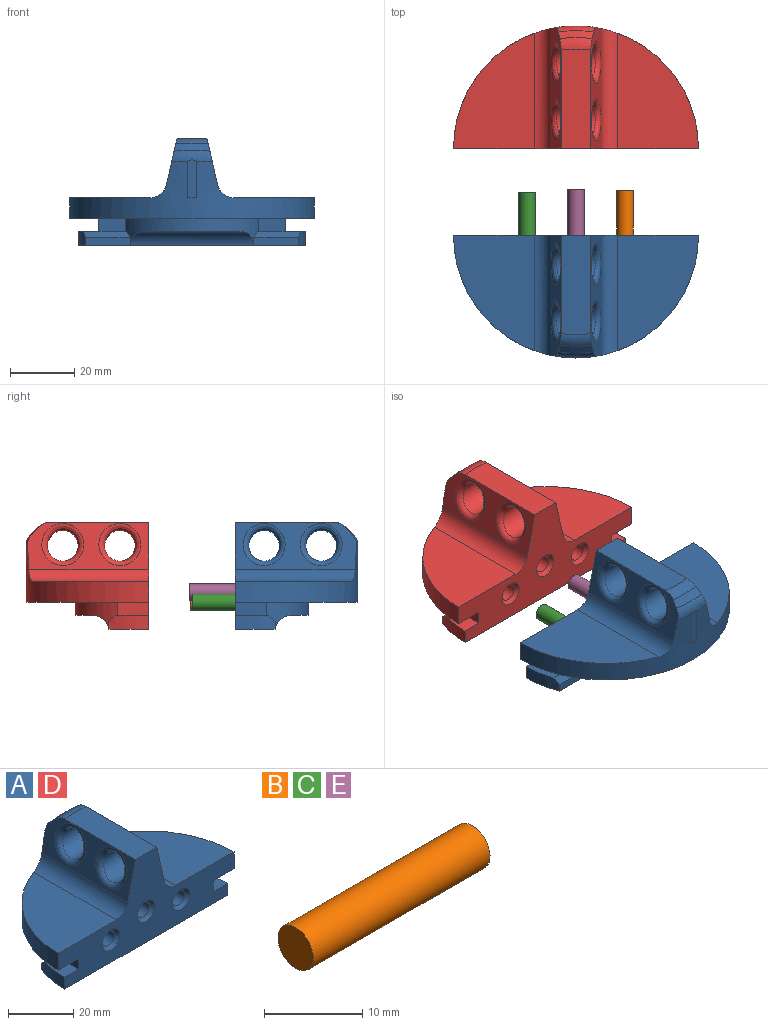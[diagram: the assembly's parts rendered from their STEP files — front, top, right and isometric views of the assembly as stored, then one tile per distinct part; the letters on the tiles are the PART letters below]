
ASSEMBLY  parts=5 mates=4
PART A: 46 faces, bbox 76.4x38.8x33.5 mm
  f0: plane 76.25x33.3mm, normal (0,-1,0), area 1152.4mm2, adj f10,f11,f12,f13,f14,f15,f16,f17
  f1: plane 29.8x5.52mm, normal (0,0,-1), area 112.7mm2, adj f6,f8
  f2: plane 2.76x0.03mm, normal (0,0,1), area 0mm2, adj f3,f25
  f3: plane 11.79x2.76mm, normal (0,1,0), area 32.2mm2, adj f2,f25,f38
  f4: plane 8.43x4.12mm, normal (0,1,0), area 34.7mm2, adj f6,f14,f15,f17
  f5: plane 8.43x4.12mm, normal (0,1,0), area 34.7mm2, adj f6,f13,f16,f17
  f6: cylinder r=22.86mm len=41.56mm, axis (0,0,-1), area 232mm2, adj f1,f4,f5,f7,f8,f9,f13,f14
  f7: plane 13.83x2.46mm, normal (0,1,0), area 34.1mm2, adj f6,f10,f11,f28
  f8: cylinder r=5.08mm len=38.53mm, axis (1,0,0), area 257.8mm2, adj f1,f6,f10
  f9: plane 13.83x2.46mm, normal (0,1,0), area 34.1mm2, adj f6,f10,f12,f27
  f10: plane 70.61x12.31mm, normal (0,0,-1), area 851mm2, adj f0,f7,f8,f9,f11,f12
  f11: cylinder r=35.31mm len=12.31mm, axis (0,0,-1), area 53mm2, adj f0,f7,f10,f13,f28
  f12: cylinder r=35.31mm len=12.31mm, axis (0,0,-1), area 53mm2, adj f0,f9,f10,f14,f27
  f13: plane 14.95x10.4mm, normal (0,0,1), area 65.6mm2, adj f0,f5,f6,f11,f16,f28
  f14: plane 14.95x10.4mm, normal (0,0,1), area 65.6mm2, adj f0,f4,f6,f12,f15,f27
  f15: plane 9.53x4.12mm, normal (-1,0,0), area 39.2mm2, adj f0,f4,f14,f17
  f16: plane 9.53x4.12mm, normal (1,0,0), area 39.2mm2, adj f0,f5,f13,f17
  f17: plane 76.25x38.13mm, normal (0,0,-1), area 1328.4mm2, adj f0,f4,f5,f6,f15,f16,f25
  f18: cylinder r=5.08mm len=37.28mm, axis (0,-1,0), area 249.8mm2, adj f0,f19,f20,f25
  f19: plane 37.78x14.7mm, normal (0.97,0,0.22), area 270mm2, adj f0,f18,f24,f25,f26,f38,f39,f42
  f20: plane 35.86x25.19mm, normal (0,0,1), area 658.2mm2, adj f0,f18,f25
  f21: cylinder r=5.08mm len=37.28mm, axis (0,1,0), area 249.8mm2, adj f0,f22,f23,f25
  f22: plane 37.78x14.7mm, normal (-0.97,0,0.22), area 270mm2, adj f0,f21,f24,f25,f26,f38,f39,f43
  f23: plane 35.86x25.19mm, normal (0,0,1), area 658.2mm2, adj f0,f21,f25
  f24: plane 30.94x9.27mm, normal (0,0,1), area 285.8mm2, adj f0,f19,f22,f39
  f25: cylinder r=38.12mm len=76.25mm, axis (0,0,-1), area 908.5mm2, adj f0,f2,f3,f17,f18,f19,f20,f21
  f26: cone r=33.04mm half-angle=45deg, axis (0,0,-1), area 31.2mm2, adj f19,f22,f38,f39
  f27: plane 14.5x1.93mm, normal (0,0.71,0.71), area 36.6mm2, adj f6,f9,f12,f14
  f28: plane 14.5x1.93mm, normal (0,0.71,0.71), area 36.6mm2, adj f6,f7,f11,f13
  f29: cylinder r=2.67mm len=11.56mm, axis (0,-1,0), area 193.7mm2, adj f30,f31
  f30: cone r=2.67mm half-angle=45deg, axis (0,-1,0), area 32.9mm2, adj f0,f29
  f31: cone r=0mm half-angle=59deg, axis (0,-1,0), area 26.1mm2, adj f29
  f32: cylinder r=2.67mm len=11.56mm, axis (0,-1,0), area 193.7mm2, adj f33,f34
  f33: cone r=2.67mm half-angle=45deg, axis (0,-1,0), area 32.9mm2, adj f0,f32
  f34: cone r=0mm half-angle=59deg, axis (0,-1,0), area 26.1mm2, adj f32
  f35: cylinder r=2.67mm len=11.56mm, axis (0,-1,0), area 193.7mm2, adj f36,f37
  f36: cone r=2.67mm half-angle=45deg, axis (0,-1,0), area 32.9mm2, adj f0,f35
  f37: cone r=0mm half-angle=59deg, axis (0,-1,0), area 26.1mm2, adj f35
  f38: torus R=33.04mm, axis (0,0,1), area 46.3mm2, adj f3,f19,f22,f25,f26
  f39: torus R=30.94mm, axis (0,0,1), area 38.1mm2, adj f19,f22,f24,f26
  f40: cylinder r=4.76mm len=12mm, axis (-1,0,0), area 268.4mm2, adj f44,f45
  f41: cylinder r=4.76mm len=12mm, axis (-1,0,0), area 268.4mm2, adj f42,f43
  f42: bspline ~13.08x13.08mm, area 96.4mm2, adj f19,f41
  f43: bspline ~13.08x13.08mm, area 96.4mm2, adj f22,f41
  f44: bspline ~13.08x13.08mm, area 96.4mm2, adj f19,f40
  f45: bspline ~13.08x13.08mm, area 96.4mm2, adj f22,f40
PART B: 3 faces, bbox 25.4x5.1x5.1 mm
  f0: cylinder r=2.54mm len=25.4mm, axis (-1,0,0), area 405.4mm2, adj f1,f2
  f1: plane 5.08x5.08mm, normal (1,0,0), area 20.3mm2, adj f0
  f2: plane 5.08x5.08mm, normal (-1,0,0), area 20.3mm2, adj f0
PART C: same geometry as B
PART D: same geometry as A
PART E: same geometry as B
PLACE A rot(axis=(0,0,-1),180deg) t=(-37.29,-65.9,-72.2)mm
PLACE B rot(axis=(-0.58,-0.58,0.58),120deg) t=(-22.05,-77.36,-72.2)mm
PLACE C rot(axis=(-0.58,-0.58,0.58),120deg) t=(-52.53,-77.95,-72.2)mm
PLACE D t=(-37.29,-38.83,-72.2)mm
PLACE E rot(axis=(-0.58,-0.58,0.58),120deg) t=(-37.29,-76.94,-69.03)mm
MATE cylindrical C.f0 <-> D.f29  axis (0,-1,0) through (-52.53,-65.25,-72.2)mm
MATE cylindrical B.f0 <-> D.f35  axis (0,-1,0) through (-22.05,-64.66,-72.2)mm
MATE cylindrical E.f0 <-> D.f32  axis (0,-1,0) through (-37.29,-64.24,-69.03)mm
MATE cylindrical A.f32 <-> D.f32  axis (0,1,0) through (-37.29,-67.04,-69.03)mm
